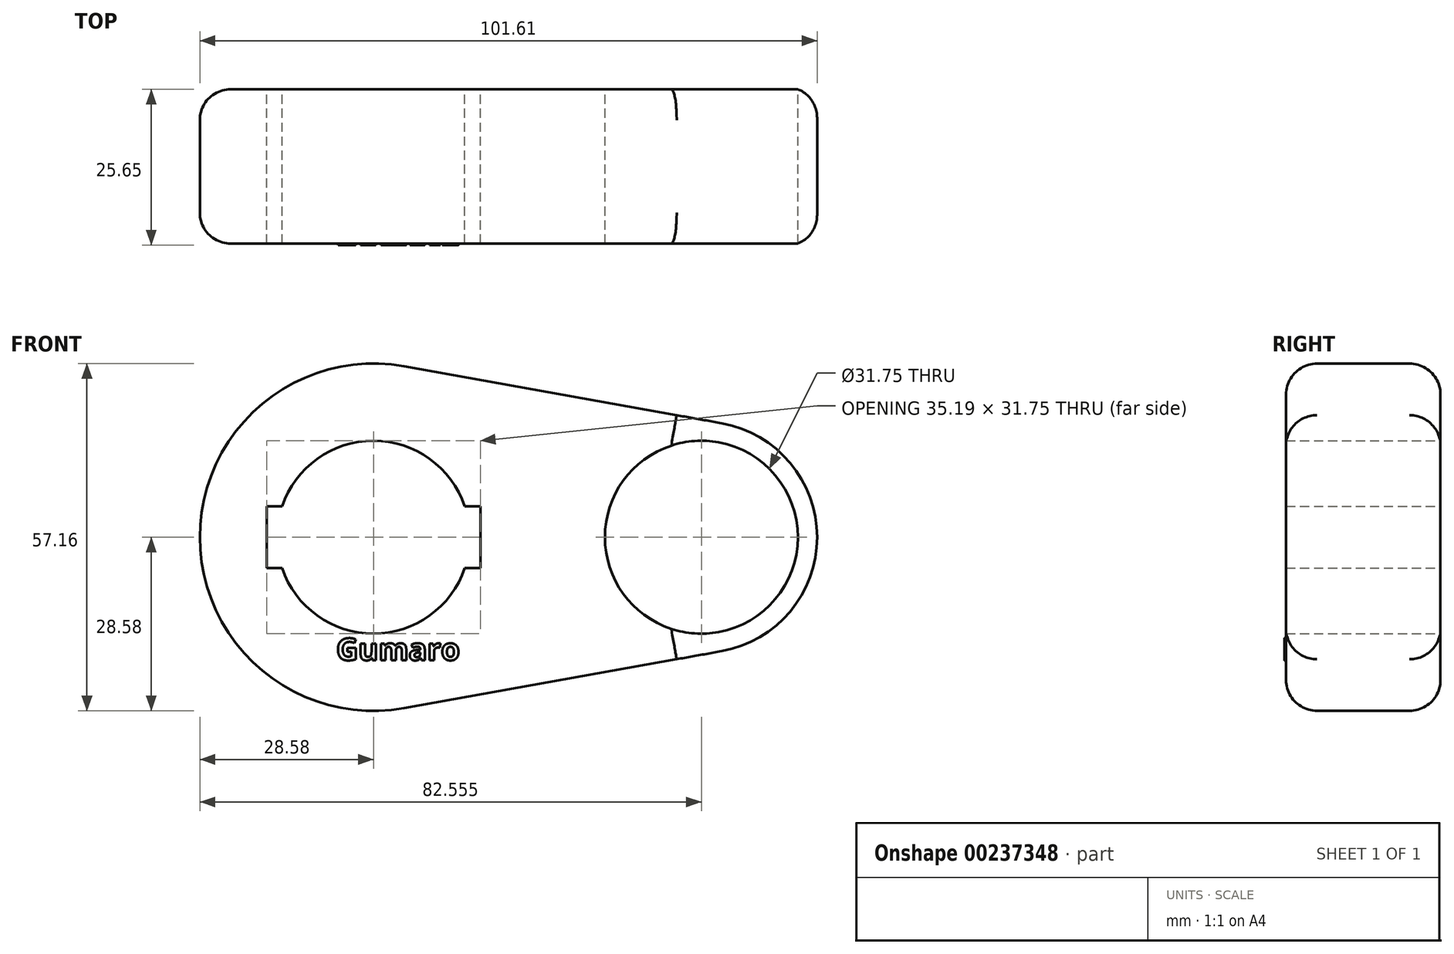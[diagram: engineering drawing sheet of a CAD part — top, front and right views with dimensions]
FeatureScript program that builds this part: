
annotation { "Feature Type Name" : "Feature", "Feature Type Description" : "" }
export const myFeature = defineFeature(function(context is Context, id is Id, definition is map)
    precondition{}
    {
        {
            var Q0;
            Q0=qCreatedBy(makeId("Front.planeOp"),FACE);
            var sketch = newSketch(context, id + "F0", { "sketchPlane" : qUnion([Q0])});
            skCircle(sketch, "E0", {"center": v(0, 0) * mm, "radius": 28.58 * mm});
            skCircle(sketch, "E1", {"center": v(53.98, 0) * mm, "radius": 19.05 * mm});
            skLineSegment(sketch, "E2", {"start": v(5.04, 28.13) * mm, "end": v(57.34, 18.75) * mm});
            skLineSegment(sketch, "E3", {"start": v(57.34, -18.75) * mm, "end": v(5.04, -28.13) * mm});
            skCircle(sketch, "E4", {"center": v(0, 0) * mm, "radius": 15.88 * mm});
            skCircle(sketch, "E5", {"center": v(53.98, 0) * mm, "radius": 15.88 * mm});
            skLineSegment(sketch, "E6.bottom", {"start": v(-17.6, -5.08) * mm, "end": v(17.6, -5.08) * mm});
            skLineSegment(sketch, "E6.top", {"start": v(-17.6, 5.08) * mm, "end": v(17.6, 5.08) * mm});
            skLineSegment(sketch, "E6.left", {"start": v(-17.6, -5.08) * mm, "end": v(-17.6, 5.08) * mm});
            skLineSegment(sketch, "E6.right", {"start": v(17.6, -5.08) * mm, "end": v(17.6, 5.08) * mm});
            skSolve(sketch);
        }
        {
            var Q0;
            {var subQ11=sQuery(id+"F0.wireOp",EDGE,"E6.left");Q0=makeQuery(id+"F0.imprint","IMPRINT",FACE,{"disambiguationData":[TD([[makeQuery(id+"F0.imprint","IMPRINT",EDGE,{"derivedFrom":subQ11}),1.0]])]});}
            extrude(context, id + "F1", {"entities" : qUnion([Q0]), "depth" : 25.4 * mm});
        }
        {
            var Q0;
            Q0 = qSketchRegion(id + "F0", true);
            extrude(context, id + "F2", {"entities" : qUnion([Q0]), "operationType" : NewBodyOperationType.ADD, "depth" : 25.4 * mm});
        }
        {
            var Q0;
            Q0=makeQuery(id+"F1.opExtrude","CAP_EDGE",EDGE,{"disambiguationData":[OSD([sQuery(id+"F0.wireOp",EDGE,"E0")])],"isStart":false});
            var Q1;
            Q1=makeQuery(id+"F2.opExtrude","CAP_EDGE",EDGE,{"disambiguationData":[OSD([sQuery(id+"F0.wireOp",EDGE,"E2")])],"isStart":false});
            var Q2;
            Q2=makeQuery(id+"F2.opExtrude","CAP_EDGE",EDGE,{"disambiguationData":[OSD([sQuery(id+"F0.wireOp",EDGE,"E3")])],"isStart":false});
            var Q3;
            Q3=makeQuery(id+"F2.opExtrude","CAP_EDGE",EDGE,{"disambiguationData":[OSD([sQuery(id+"F0.wireOp",EDGE,"E1")])],"isStart":false});
            var Q4;
            Q4=makeQuery(id+"F2.opExtrude","CAP_EDGE",EDGE,{"disambiguationData":[OSD([sQuery(id+"F0.wireOp",EDGE,"E3")])],"isStart":true});
            var Q5;
            Q5=makeQuery(id+"F1.opExtrude","CAP_EDGE",EDGE,{"disambiguationData":[OSD([sQuery(id+"F0.wireOp",EDGE,"E0")])],"isStart":true});
            var Q6;
            Q6=makeQuery(id+"F2.opExtrude","CAP_EDGE",EDGE,{"disambiguationData":[OSD([sQuery(id+"F0.wireOp",EDGE,"E2")])],"isStart":true});
            var Q7;
            Q7=makeQuery(id+"F2.opExtrude","CAP_EDGE",EDGE,{"disambiguationData":[OSD([sQuery(id+"F0.wireOp",EDGE,"E1")])],"isStart":true});
            fillet(context, id + "F3", {"entities" : qUnion([Q0, Q1, Q2, Q3, Q4, Q5, Q6, Q7]), "radius" : 5.08 * mm, "tangentPropagation" : true, "allowEdgeOverflow" : false});
        }
        {
            var Q0;
            {var subQ0=sQuery(id+"F0.wireOp",EDGE,"E6.right");var subQ1=sQuery(id+"F0.wireOp",EDGE,"E6.left");var subQ2=sQuery(id+"F0.wireOp",EDGE,"E6.top");var subQ3=sQuery(id+"F0.wireOp",EDGE,"E6.bottom");var subQ4=sQuery(id+"F0.wireOp",EDGE,"E4");var subQ5=sQuery(id+"F0.wireOp",EDGE,"E0");Q0=makeQuery(id+"F2.boolean.opBoolean","MERGE",FACE,{"derivedFrom":[makeQuery(id+"F1.opExtrude","CAP_FACE",FACE,{"disambiguationData":[OSD([subQ5,subQ4,subQ3,subQ2,subQ1,subQ0])],"isStart":false}),makeQuery(id+"F2.opExtrude","CAP_FACE",FACE,{"disambiguationData":[OSD([subQ5,sQuery(id+"F0.wireOp",EDGE,"E1"),sQuery(id+"F0.wireOp",EDGE,"E2"),sQuery(id+"F0.wireOp",EDGE,"E3"),subQ4,sQuery(id+"F0.wireOp",EDGE,"E5"),subQ3,subQ2,subQ1,subQ0])],"isStart":false})]});}
            var sketch = newSketch(context, id + "F4", { "sketchPlane" : qUnion([Q0])});
            skText(sketch, "E7", { "text": "Gumaro", "fontName": "OpenSans-Bold.ttf"});
            const initialGuessF4  = {"E7": [-0.00614, -0.02025, 1, 0, 0.00363]};
            skSetInitialGuess(sketch, initialGuessF4);
            skSolve(sketch);
        }
        {
            var Q0;
            Q0 = qSketchRegion(id + "F4", true);
            extrude(context, id + "F5", {"entities" : qUnion([Q0]), "operationType" : NewBodyOperationType.ADD, "depth" : 0.25 * mm});
        }
    });
